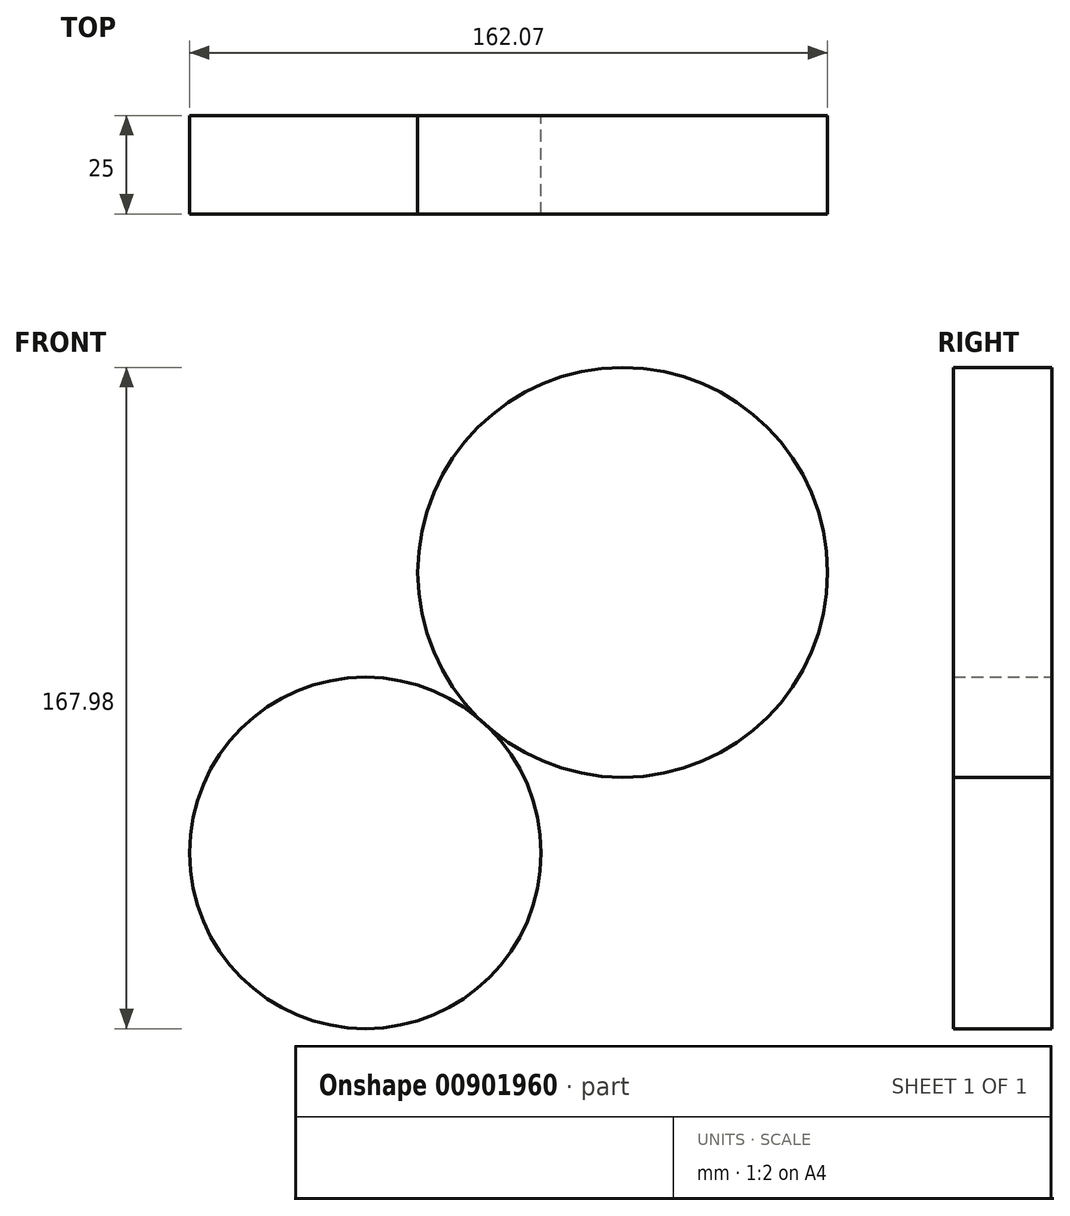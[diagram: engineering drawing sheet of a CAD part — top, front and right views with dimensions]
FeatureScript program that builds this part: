
annotation { "Feature Type Name" : "Feature", "Feature Type Description" : "" }
export const myFeature = defineFeature(function(context is Context, id is Id, definition is map)
    precondition{}
    {
        {
            var Q0;
            Q0=qCreatedBy(makeId("Front.planeOp"),FACE);
            var sketch = newSketch(context, id + "F0", { "sketchPlane" : qUnion([Q0])});
            skCircle(sketch, "E0", {"center": v(22.28, 23.29) * mm, "radius": 52.05 * mm});
            skCircle(sketch, "E1", {"center": v(-43.08, -47.98) * mm, "radius": 44.65 * mm});
            skSolve(sketch);
        }
        {
            var Q0;
            Q0 = qSketchRegion(id + "F0", true);
            extrude(context, id + "F1", {"entities" : qUnion([Q0]), "depth" : 25 * mm, "offsetDistance" : 25 * mm});
        }
    });
